# Revit family: AFX-Palmer-LED_Vanity-1
name_source: partatom
category: Lighting Fixtures
units: mm (PartAtom-declared; Revit-internal decimal feet)

## family parameters
Cut with Voids When Loaded = No
Host = Face
Light Source = Yes
Part Type = Normal
Room Calculation Point = No
Round Connector Dimension = Use Diameter
Shared = No

## types (3) — shared parameters
Apparent Load = 0 VA
Assembly Code = D5020200
Cap Finish = AFX - Black Steel
Color Filter = 16777215
Colour Rendering Index = 80
Default Elevation = 48"
Depth = 3 1/2"
Diffuser Finish = AFX - White Acrylic
Dimming Lamp Color Temperature Shift = <None>
Emit Shape Visible in Rendering = No
Emit from Rectangle Length = 5"
Height = 5 1/2"
Housing Finish = AFX - Black Steel
Keynote = 12500
Manufacturer = AFX Inc
Product Documentation Link = https://www.afxinc.com
Revit File Built By = https://servex-us.com
Supports Finish = AFX - Black Steel
Sustainability = https://lamprecycle.org
Tilt Angle = 90.00°
Type Comments = Palmer
URL = https://www.afxinc.com
Voltage = 120 V
Wattage Comments = 25W

## per-type parameters (varying)
| type | Description | Emit from Rectangle Width | Length | Photometric Web File |
| PLMV2406LAJUDBK | LED Vanity - 24"L x 5 1/2"H x 3 1/2"D | 23 3/4" | 24" | PLMV2406LAJUDBK_3000K_IES.IES |
| PLMV3606LAJUDBK | LED Vanity - 36"L x 5 1/2"H x 3 1/2"D | 35 3/4" | 36" | PLMV3606LAJUDBK_3000K_IES.IES |
| PLMV4806LAJUDBK | LED Vanity - 48"L x 5 1/2"H x 3 1/2"D | 47 3/4" | 48" | PLMV4806LAJUDSN_3000K_IES.IES |

note: column(s) folded — value = type name in every type: Model

## geometry (parser evidence)
native form markers: Sweep x2
no freeform markers — native parametric forms only
